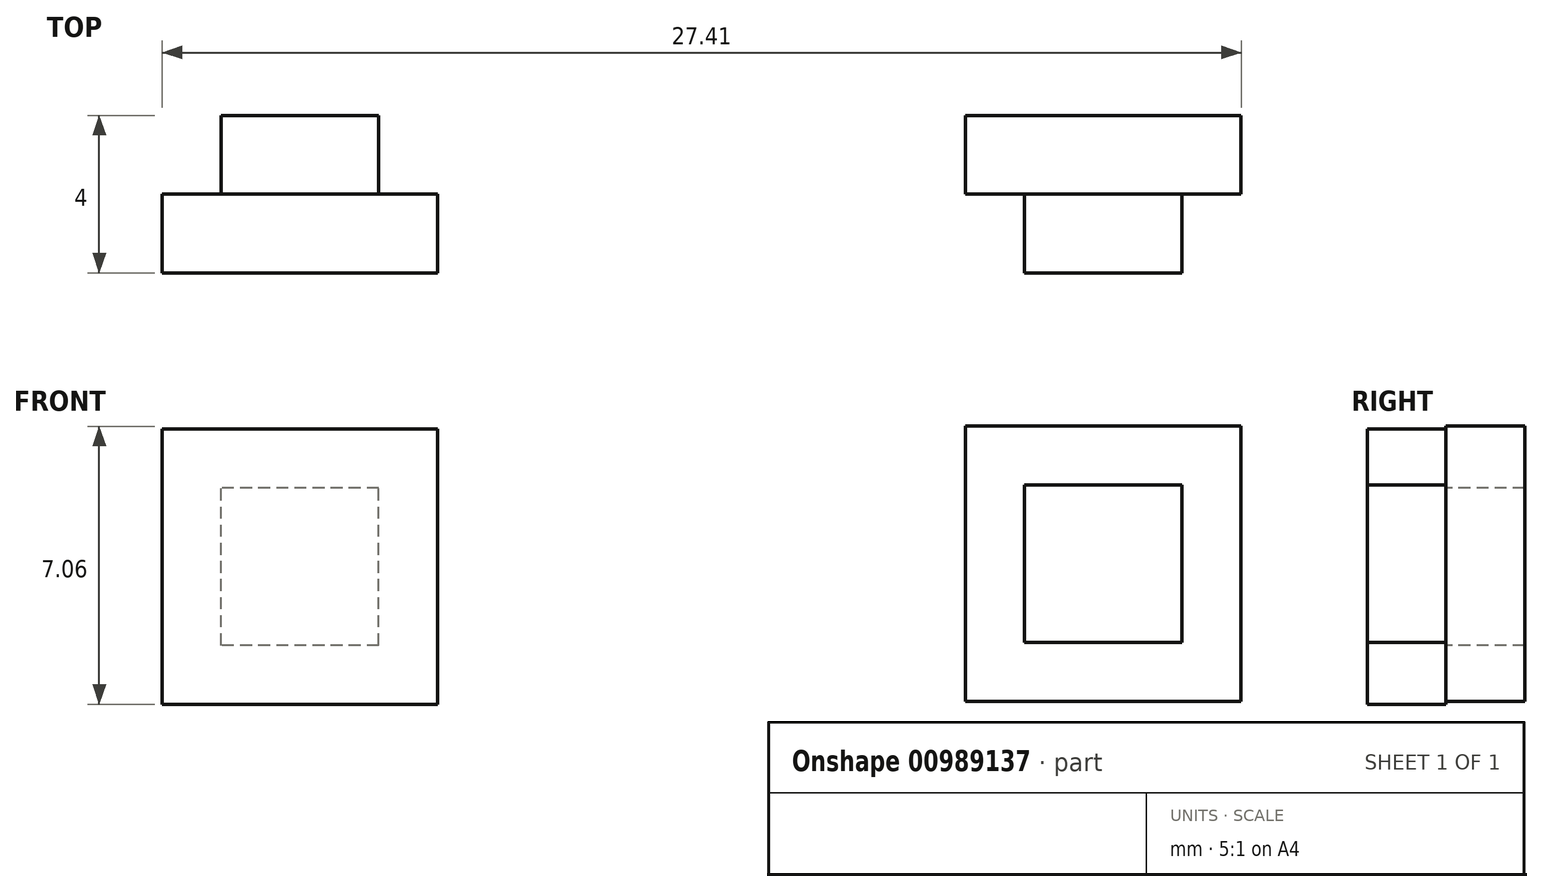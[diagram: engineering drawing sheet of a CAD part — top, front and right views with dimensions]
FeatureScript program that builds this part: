
annotation { "Feature Type Name" : "Feature", "Feature Type Description" : "" }
export const myFeature = defineFeature(function(context is Context, id is Id, definition is map)
    precondition{}
    {
        {
            var Q0;
            Q0=qCreatedBy(makeId("Front.planeOp"),FACE);
            var sketch = newSketch(context, id + "F0", { "sketchPlane" : qUnion([Q0])});
            skLineSegment(sketch, "E0.bottom", {"start": v(2.06, -2.05) * mm, "end": v(-1.94, -2.05) * mm});
            skLineSegment(sketch, "E0.top", {"start": v(2.06, 1.95) * mm, "end": v(-1.94, 1.95) * mm});
            skLineSegment(sketch, "E0.left", {"start": v(2.06, -2.05) * mm, "end": v(2.06, 1.95) * mm});
            skLineSegment(sketch, "E0.right", {"start": v(-1.94, -2.05) * mm, "end": v(-1.94, 1.95) * mm});
            skLineSegment(sketch, "E1.bottom", {"start": v(3.56, -3.55) * mm, "end": v(-3.44, -3.55) * mm});
            skLineSegment(sketch, "E1.top", {"start": v(3.56, 3.45) * mm, "end": v(-3.44, 3.45) * mm});
            skLineSegment(sketch, "E1.left", {"start": v(3.56, -3.55) * mm, "end": v(3.56, 3.45) * mm});
            skLineSegment(sketch, "E1.right", {"start": v(-3.44, -3.55) * mm, "end": v(-3.44, 3.45) * mm});
            skLineSegment(sketch, "E2.bottom", {"start": v(-18.35, -2.11) * mm, "end": v(-22.35, -2.11) * mm});
            skLineSegment(sketch, "E2.top", {"start": v(-18.35, 1.89) * mm, "end": v(-22.35, 1.89) * mm});
            skLineSegment(sketch, "E2.left", {"start": v(-18.35, -2.11) * mm, "end": v(-18.35, 1.89) * mm});
            skLineSegment(sketch, "E2.right", {"start": v(-22.35, -2.11) * mm, "end": v(-22.35, 1.89) * mm});
            skLineSegment(sketch, "E3.bottom", {"start": v(-16.85, -3.61) * mm, "end": v(-23.85, -3.61) * mm});
            skLineSegment(sketch, "E3.top", {"start": v(-16.85, 3.39) * mm, "end": v(-23.85, 3.39) * mm});
            skLineSegment(sketch, "E3.left", {"start": v(-16.85, -3.61) * mm, "end": v(-16.85, 3.39) * mm});
            skLineSegment(sketch, "E3.right", {"start": v(-23.85, -3.61) * mm, "end": v(-23.85, 3.39) * mm});
            skSolve(sketch);
        }
        {
            var Q0;
            Q0=makeQuery(id+"F0.imprint","IMPRINT",FACE,{"disambiguationData":[TD([[makeQuery(id+"F0.imprint","IMPRINT",EDGE,{"derivedFrom":sQuery(id+"F0.wireOp",EDGE,"E0.bottom")}),-1.0]])]});
            extrude(context, id + "F1", {"entities" : qUnion([Q0]), "depth" : 2 * mm, "offsetDistance" : 25.4 * mm});
        }
        {
            var Q0;
            Q0=makeQuery(id+"F0.imprint","IMPRINT",FACE,{"disambiguationData":[TD([[makeQuery(id+"F0.imprint","IMPRINT",EDGE,{"derivedFrom":sQuery(id+"F0.wireOp",EDGE,"E0.bottom")}),1.0]])]});
            var Q1;
            Q1=makeQuery(id+"F0.imprint","IMPRINT",FACE,{"disambiguationData":[TD([[makeQuery(id+"F0.imprint","IMPRINT",EDGE,{"derivedFrom":sQuery(id+"F0.wireOp",EDGE,"E0.bottom")}),-1.0]])]});
            extrude(context, id + "F2", {"entities" : qUnion([Q0, Q1]), "operationType" : NewBodyOperationType.ADD, "oppositeDirection" : true, "depth" : 2 * mm, "offsetDistance" : 25.4 * mm});
        }
        {
            var Q0;
            Q0=makeQuery(id+"F0.imprint","IMPRINT",FACE,{"disambiguationData":[TD([[makeQuery(id+"F0.imprint","IMPRINT",EDGE,{"derivedFrom":sQuery(id+"F0.wireOp",EDGE,"E2.bottom")}),-1.0]])]});
            extrude(context, id + "F3", {"entities" : qUnion([Q0]), "oppositeDirection" : true, "depth" : 2 * mm, "offsetDistance" : 25.4 * mm});
        }
        {
            var Q0;
            Q0=makeQuery(id+"F0.imprint","IMPRINT",FACE,{"disambiguationData":[TD([[makeQuery(id+"F0.imprint","IMPRINT",EDGE,{"derivedFrom":sQuery(id+"F0.wireOp",EDGE,"E2.bottom")}),1.0]])]});
            var Q1;
            Q1=makeQuery(id+"F0.imprint","IMPRINT",FACE,{"disambiguationData":[TD([[makeQuery(id+"F0.imprint","IMPRINT",EDGE,{"derivedFrom":sQuery(id+"F0.wireOp",EDGE,"E2.bottom")}),-1.0]])]});
            extrude(context, id + "F4", {"entities" : qUnion([Q0, Q1]), "operationType" : NewBodyOperationType.ADD, "depth" : 2 * mm, "offsetDistance" : 25.4 * mm});
        }
    });
